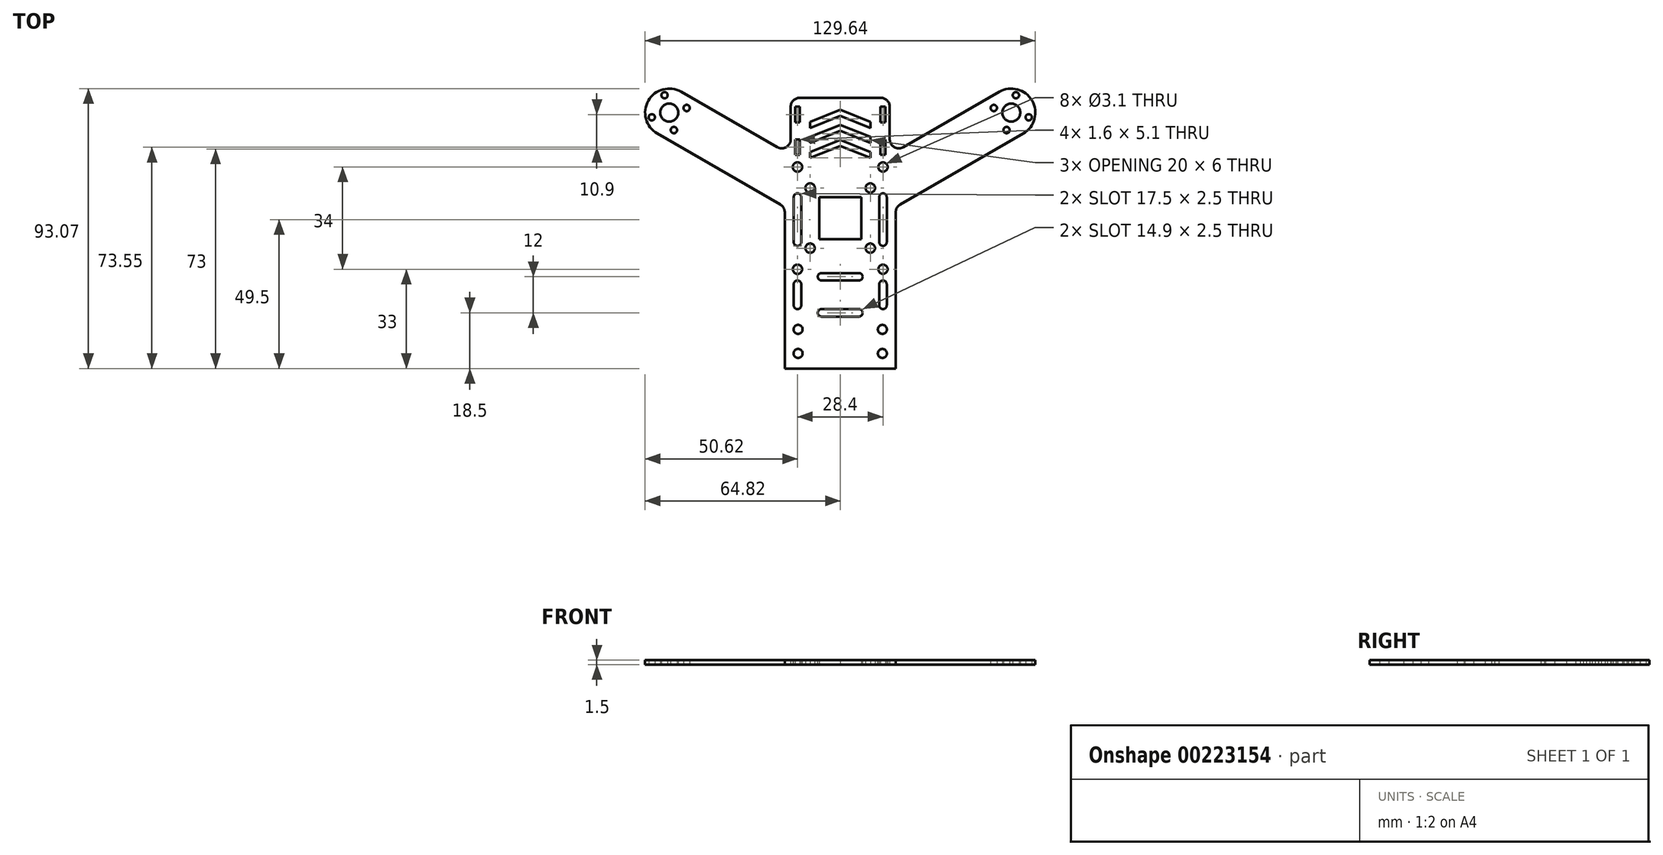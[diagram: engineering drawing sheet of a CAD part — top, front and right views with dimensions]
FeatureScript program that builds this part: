
annotation { "Feature Type Name" : "Feature", "Feature Type Description" : "" }
export const myFeature = defineFeature(function(context is Context, id is Id, definition is map)
    precondition{}
    {
        {
            var Q0;
            Q0=qCreatedBy(makeId("Top.planeOp"),FACE);
            var sketch = newSketch(context, id + "F0", { "sketchPlane" : qUnion([Q0])});
            skLineSegment(sketch, "E0.bottom", {"start": v(16.45, -32) * mm, "end": v(-16.45, -32) * mm});
            skLineSegment(sketch, "E0.top", {"start": v(16.45, 32) * mm, "end": v(-16.45, 32) * mm});
            skLineSegment(sketch, "E0.left", {"start": v(16.45, -32) * mm, "end": v(16.45, 32) * mm});
            skLineSegment(sketch, "E0.right", {"start": v(-16.45, -32) * mm, "end": v(-16.45, 32) * mm});
            skPoint(sketch, "E0.middle", {"position": v(0, 0) * mm});
            skLineSegment(sketch, "E1.bottom", {"start": v(-15, 29) * mm, "end": v(-13.4, 29) * mm});
            skLineSegment(sketch, "E1.top", {"start": v(-15, 23.9) * mm, "end": v(-13.4, 23.9) * mm});
            skLineSegment(sketch, "E1.left", {"start": v(-15, 29) * mm, "end": v(-15, 23.9) * mm});
            skLineSegment(sketch, "E1.right", {"start": v(-13.4, 29) * mm, "end": v(-13.4, 23.9) * mm});
            skLineSegment(sketch, "E2.bottom", {"start": v(15, 29) * mm, "end": v(13.4, 29) * mm});
            skLineSegment(sketch, "E2.top", {"start": v(15, 23.9) * mm, "end": v(13.4, 23.9) * mm});
            skLineSegment(sketch, "E2.left", {"start": v(15, 29) * mm, "end": v(15, 23.9) * mm});
            skLineSegment(sketch, "E2.right", {"start": v(13.4, 29) * mm, "end": v(13.4, 23.9) * mm});
            skLineSegment(sketch, "E3.bottom", {"start": v(-15, 18.1) * mm, "end": v(-13.4, 18.1) * mm});
            skLineSegment(sketch, "E3.top", {"start": v(-15, 13) * mm, "end": v(-13.4, 13) * mm});
            skLineSegment(sketch, "E3.left", {"start": v(-15, 18.1) * mm, "end": v(-15, 13) * mm});
            skLineSegment(sketch, "E3.right", {"start": v(-13.4, 18.1) * mm, "end": v(-13.4, 13) * mm});
            skLineSegment(sketch, "E4.bottom", {"start": v(13.4, 18.1) * mm, "end": v(15, 18.1) * mm});
            skLineSegment(sketch, "E4.top", {"start": v(13.4, 13) * mm, "end": v(15, 13) * mm});
            skLineSegment(sketch, "E4.left", {"start": v(13.4, 18.1) * mm, "end": v(13.4, 13) * mm});
            skLineSegment(sketch, "E4.right", {"start": v(15, 18.1) * mm, "end": v(15, 13) * mm});
            skCircle(sketch, "E5", {"center": v(-10, 2) * mm, "radius": 1.55 * mm});
            skCircle(sketch, "E6", {"center": v(10, 2) * mm, "radius": 1.55 * mm});
            skCircle(sketch, "E7", {"center": v(10, -18) * mm, "radius": 1.55 * mm});
            skCircle(sketch, "E8", {"center": v(-10, -18) * mm, "radius": 1.55 * mm});
            skLineSegment(sketch, "E9", {"start": v(0, 28) * mm, "end": v(-10, 24) * mm});
            skLineSegment(sketch, "E10", {"start": v(-10, 24) * mm, "end": v(-10, 22) * mm});
            skLineSegment(sketch, "E11", {"start": v(-10, 22) * mm, "end": v(0, 26) * mm});
            skLineSegment(sketch, "E12", {"start": v(0, 26) * mm, "end": v(10, 22) * mm});
            skLineSegment(sketch, "E13", {"start": v(10, 22) * mm, "end": v(10, 24) * mm});
            skLineSegment(sketch, "E14", {"start": v(10, 24) * mm, "end": v(0, 28) * mm});
            skLineSegment(sketch, "E15", {"start": v(0, 23) * mm, "end": v(-10, 19) * mm});
            skLineSegment(sketch, "E16", {"start": v(-10, 19) * mm, "end": v(-10, 17) * mm});
            skLineSegment(sketch, "E17", {"start": v(-10, 17) * mm, "end": v(0, 21) * mm});
            skLineSegment(sketch, "E18", {"start": v(0, 21) * mm, "end": v(10, 17) * mm});
            skLineSegment(sketch, "E19", {"start": v(10, 17) * mm, "end": v(10, 19) * mm});
            skLineSegment(sketch, "E20", {"start": v(10, 19) * mm, "end": v(0, 23) * mm});
            skLineSegment(sketch, "E21", {"start": v(0, 18) * mm, "end": v(-10, 14) * mm});
            skLineSegment(sketch, "E22", {"start": v(-10, 14) * mm, "end": v(-10, 12) * mm});
            skLineSegment(sketch, "E23", {"start": v(-10, 12) * mm, "end": v(0, 16) * mm});
            skLineSegment(sketch, "E24", {"start": v(0, 16) * mm, "end": v(10, 12) * mm});
            skLineSegment(sketch, "E25", {"start": v(10, 12) * mm, "end": v(10, 14) * mm});
            skLineSegment(sketch, "E26", {"start": v(10, 14) * mm, "end": v(0, 18) * mm});
            skCircle(sketch, "E27", {"center": v(14.2, 9) * mm, "radius": 1.55 * mm});
            skPoint(sketch, "E27.centerSnap0", {"position": v(14.2, 13) * mm});
            skCircle(sketch, "E28", {"center": v(-14.2, 9) * mm, "radius": 1.55 * mm});
            skPoint(sketch, "E28.centerSnap0", {"position": v(-14.2, 13) * mm});
            skCircle(sketch, "E29", {"center": v(-56.82, 27.07) * mm, "radius": 38.5 * mm, "construction": true});
            skCircle(sketch, "E30", {"center": v(56.82, 27.07) * mm, "radius": 38.5 * mm, "construction": true});
            skLineSegment(sketch, "E31", {"start": v(-52.82, 34) * mm, "end": v(-16.45, 13) * mm});
            skLineSegment(sketch, "E32", {"start": v(-52.82, 34) * mm, "end": v(-56.82, 27.07) * mm, "construction": true});
            skLineSegment(sketch, "E33", {"start": v(16.45, 13) * mm, "end": v(52.82, 34) * mm});
            skPoint(sketch, "E33.startSnap0", {"position": v(-10, 13) * mm});
            skLineSegment(sketch, "E34", {"start": v(52.82, 34) * mm, "end": v(56.82, 27.07) * mm, "construction": true});
            skArc(sketch, "E35", {"start": v(-52.82, 34) * mm, "mid": v(-63.75, 31.07) * mm, "end": v(-60.82, 20.14) * mm});
            skArc(sketch, "E36", {"start": v(52.82, 34) * mm, "mid": v(63.75, 31.07) * mm, "end": v(60.82, 20.14) * mm});
            skLineSegment(sketch, "E37", {"start": v(-56.82, 27.07) * mm, "end": v(-60.82, 20.14) * mm, "construction": true});
            skLineSegment(sketch, "E38", {"start": v(-60.82, 20.14) * mm, "end": v(-16.45, -5.48) * mm});
            skLineSegment(sketch, "E39", {"start": v(60.82, 20.14) * mm, "end": v(16.45, -5.48) * mm});
            skCircle(sketch, "E40", {"center": v(-56.82, 27.07) * mm, "radius": 3 * mm});
            skCircle(sketch, "E41", {"center": v(56.82, 27.07) * mm, "radius": 3 * mm});
            skCircle(sketch, "E42", {"center": v(56.82, 27.07) * mm, "radius": 6 * mm, "construction": true});
            skCircle(sketch, "E43", {"center": v(-56.82, 27.07) * mm, "radius": 6 * mm, "construction": true});
            skLineSegment(sketch, "E44", {"start": v(-59.65, 37.63) * mm, "end": v(-53.6, 15.03) * mm, "construction": true});
            skLineSegment(sketch, "E45", {"start": v(-69.83, 23.59) * mm, "end": v(-44.54, 30.36) * mm, "construction": true});
            skCircle(sketch, "E46", {"center": v(-58.38, 32.87) * mm, "radius": 1.05 * mm});
            skCircle(sketch, "E47", {"center": v(-51.03, 28.62) * mm, "radius": 1.05 * mm});
            skCircle(sketch, "E48", {"center": v(-62.62, 25.52) * mm, "radius": 1.05 * mm});
            skCircle(sketch, "E49", {"center": v(-55.27, 21.28) * mm, "radius": 1.05 * mm});
            skLineSegment(sketch, "E50", {"start": v(42.78, 30.83) * mm, "end": v(71.93, 23.02) * mm, "construction": true});
            skLineSegment(sketch, "E51", {"start": v(59.98, 38.85) * mm, "end": v(52.62, 11.38) * mm, "construction": true});
            skCircle(sketch, "E52", {"center": v(58.38, 32.87) * mm, "radius": 1.05 * mm});
            skCircle(sketch, "E53", {"center": v(62.62, 25.52) * mm, "radius": 1.05 * mm});
            skCircle(sketch, "E54", {"center": v(55.27, 21.28) * mm, "radius": 1.05 * mm});
            skCircle(sketch, "E55", {"center": v(51.03, 28.62) * mm, "radius": 1.05 * mm});
            skCircle(sketch, "E56", {"center": v(14.2, -25) * mm, "radius": 1.55 * mm});
            skCircle(sketch, "E57", {"center": v(-14.2, -25) * mm, "radius": 1.55 * mm});
            skLineSegment(sketch, "E58", {"start": v(16.45, -32) * mm, "end": v(16.45, -5.48) * mm});
            skLineSegment(sketch, "E59", {"start": v(18.45, -4.32) * mm, "end": v(18.45, -32) * mm});
            skLineSegment(sketch, "E60", {"start": v(18.45, -32) * mm, "end": v(16.45, -32) * mm});
            skLineSegment(sketch, "E61", {"start": v(-16.45, -32) * mm, "end": v(-16.45, -5.48) * mm});
            skLineSegment(sketch, "E62", {"start": v(-18.45, -4.32) * mm, "end": v(-18.45, -32) * mm});
            skLineSegment(sketch, "E63", {"start": v(-18.45, -32) * mm, "end": v(-16.45, -32) * mm});
            skLineSegment(sketch, "E64.bottom", {"start": v(-7, -1) * mm, "end": v(7, -1) * mm});
            skLineSegment(sketch, "E64.top", {"start": v(-7, -15) * mm, "end": v(7, -15) * mm});
            skLineSegment(sketch, "E64.left", {"start": v(-7, -1) * mm, "end": v(-7, -15) * mm});
            skLineSegment(sketch, "E64.right", {"start": v(7, -1) * mm, "end": v(7, -15) * mm});
            skLineSegment(sketch, "E65.bottom", {"start": v(-18.45, -32) * mm, "end": v(18.45, -32) * mm});
            skLineSegment(sketch, "E65.top", {"start": v(-18.45, -58) * mm, "end": v(18.45, -58) * mm});
            skLineSegment(sketch, "E65.left", {"start": v(-18.45, -32) * mm, "end": v(-18.45, -58) * mm});
            skLineSegment(sketch, "E65.right", {"start": v(18.45, -32) * mm, "end": v(18.45, -58) * mm});
            skSolve(sketch);
        }
        {
            var Q0;
            Q0 = qSketchRegion(id + "F0", true);
            extrude(context, id + "F1", {"entities" : qUnion([Q0]), "depth" : 1.5 * mm});
        }
        {
            var Q0;
            Q0=makeQuery(id+"F1.opExtrude","SWEPT_EDGE",EDGE,{"disambiguationData":[OSD([sQuery(id+"F0.wireOp",EDGE,"E0.right"),sQuery(id+"F0.wireOp",EDGE,"E31")])]});
            var Q1;
            Q1=makeQuery(id+"F1.opExtrude","SWEPT_EDGE",EDGE,{"disambiguationData":[OSD([sQuery(id+"F0.wireOp",EDGE,"E0.left"),sQuery(id+"F0.wireOp",EDGE,"E33")])]});
            var Q2;
            Q2=makeQuery(id+"F1.opExtrude","SWEPT_EDGE",EDGE,{"disambiguationData":[OSD([sQuery(id+"F0.wireOp",EDGE,"E0.left"),sQuery(id+"F0.wireOp",EDGE,"E39")])]});
            var Q3;
            Q3=makeQuery(id+"F1.opExtrude","SWEPT_EDGE",EDGE,{"disambiguationData":[OSD([sQuery(id+"F0.wireOp",EDGE,"E0.right"),sQuery(id+"F0.wireOp",EDGE,"E38")])]});
            fillet(context, id + "F2", {"entities" : qUnion([Q0, Q1, Q2, Q3]), "radius" : 3 * mm, "tangentPropagation" : true, "allowEdgeOverflow" : false});
        }
        {
            var Q0;
            Q0=makeQuery(id+"F1.opExtrude","CAP_FACE",FACE,{"disambiguationData":[OSD([sQuery(id+"F0.wireOp",EDGE,"E0.bottom"),sQuery(id+"F0.wireOp",EDGE,"E0.top"),sQuery(id+"F0.wireOp",EDGE,"E0.left"),sQuery(id+"F0.wireOp",EDGE,"E0.right"),sQuery(id+"F0.wireOp",EDGE,"E1.bottom"),sQuery(id+"F0.wireOp",EDGE,"E1.top"),sQuery(id+"F0.wireOp",EDGE,"E1.left"),sQuery(id+"F0.wireOp",EDGE,"E1.right"),sQuery(id+"F0.wireOp",EDGE,"E2.bottom"),sQuery(id+"F0.wireOp",EDGE,"E2.top"),sQuery(id+"F0.wireOp",EDGE,"E2.left"),sQuery(id+"F0.wireOp",EDGE,"E2.right"),sQuery(id+"F0.wireOp",EDGE,"E3.bottom"),sQuery(id+"F0.wireOp",EDGE,"E3.top"),sQuery(id+"F0.wireOp",EDGE,"E3.left"),sQuery(id+"F0.wireOp",EDGE,"E3.right"),sQuery(id+"F0.wireOp",EDGE,"E4.bottom"),sQuery(id+"F0.wireOp",EDGE,"E4.top"),sQuery(id+"F0.wireOp",EDGE,"E4.left"),sQuery(id+"F0.wireOp",EDGE,"E4.right"),sQuery(id+"F0.wireOp",EDGE,"E5"),sQuery(id+"F0.wireOp",EDGE,"E6"),sQuery(id+"F0.wireOp",EDGE,"E7"),sQuery(id+"F0.wireOp",EDGE,"E8"),sQuery(id+"F0.wireOp",EDGE,"E9"),sQuery(id+"F0.wireOp",EDGE,"E10"),sQuery(id+"F0.wireOp",EDGE,"E11"),sQuery(id+"F0.wireOp",EDGE,"E12"),sQuery(id+"F0.wireOp",EDGE,"E13"),sQuery(id+"F0.wireOp",EDGE,"E14"),sQuery(id+"F0.wireOp",EDGE,"E15"),sQuery(id+"F0.wireOp",EDGE,"E16"),sQuery(id+"F0.wireOp",EDGE,"E17"),sQuery(id+"F0.wireOp",EDGE,"E18"),sQuery(id+"F0.wireOp",EDGE,"E19"),sQuery(id+"F0.wireOp",EDGE,"E20"),sQuery(id+"F0.wireOp",EDGE,"E21"),sQuery(id+"F0.wireOp",EDGE,"E22"),sQuery(id+"F0.wireOp",EDGE,"E23"),sQuery(id+"F0.wireOp",EDGE,"E24"),sQuery(id+"F0.wireOp",EDGE,"E25"),sQuery(id+"F0.wireOp",EDGE,"E26"),sQuery(id+"F0.wireOp",EDGE,"E27"),sQuery(id+"F0.wireOp",EDGE,"E28"),sQuery(id+"F0.wireOp",EDGE,"E31"),sQuery(id+"F0.wireOp",EDGE,"E33"),sQuery(id+"F0.wireOp",EDGE,"E35"),sQuery(id+"F0.wireOp",EDGE,"E36"),sQuery(id+"F0.wireOp",EDGE,"E38"),sQuery(id+"F0.wireOp",EDGE,"E39"),sQuery(id+"F0.wireOp",EDGE,"E40"),sQuery(id+"F0.wireOp",EDGE,"E41"),sQuery(id+"F0.wireOp",EDGE,"E46"),sQuery(id+"F0.wireOp",EDGE,"E47"),sQuery(id+"F0.wireOp",EDGE,"E48"),sQuery(id+"F0.wireOp",EDGE,"E49"),sQuery(id+"F0.wireOp",EDGE,"E52"),sQuery(id+"F0.wireOp",EDGE,"E53"),sQuery(id+"F0.wireOp",EDGE,"E54"),sQuery(id+"F0.wireOp",EDGE,"E55"),sQuery(id+"F0.wireOp",EDGE,"E56"),sQuery(id+"F0.wireOp",EDGE,"E57"),sQuery(id+"F0.wireOp",EDGE,"E59"),sQuery(id+"F0.wireOp",EDGE,"E60"),sQuery(id+"F0.wireOp",EDGE,"E62"),sQuery(id+"F0.wireOp",EDGE,"E63")])],"isStart":false});
            var sketch = newSketch(context, id + "F3", { "sketchPlane" : qUnion([Q0])});
            skLineSegment(sketch, "E66", {"start": v(-14.2, -25) * mm, "end": v(14.2, -25) * mm, "construction": true});
            skLineSegment(sketch, "E67", {"start": v(-14.2, -1) * mm, "end": v(-14.2, -16) * mm});
            skLineSegment(sketch, "E68", {"start": v(14.2, -1) * mm, "end": v(14.2, -16) * mm});
            skArc(sketch, "E69.0.startCap", {"start": v(-15.45, -1) * mm, "mid": v(-14.2, 0.25) * mm, "end": v(-12.95, -1) * mm});
            skArc(sketch, "E69.0.endCap", {"start": v(-12.95, -16) * mm, "mid": v(-14.2, -17.25) * mm, "end": v(-15.45, -16) * mm});
            skLineSegment(sketch, "E69.0.left", {"start": v(-12.95, -1) * mm, "end": v(-12.95, -16) * mm});
            skLineSegment(sketch, "E69.0.right", {"start": v(-15.45, -1) * mm, "end": v(-15.45, -16) * mm});
            skArc(sketch, "E70.0.startCap", {"start": v(12.95, -1) * mm, "mid": v(14.2, 0.25) * mm, "end": v(15.45, -1) * mm});
            skArc(sketch, "E70.0.endCap", {"start": v(15.45, -16) * mm, "mid": v(14.2, -17.25) * mm, "end": v(12.95, -16) * mm});
            skLineSegment(sketch, "E70.0.left", {"start": v(15.45, -1) * mm, "end": v(15.45, -16) * mm});
            skLineSegment(sketch, "E70.0.right", {"start": v(12.95, -1) * mm, "end": v(12.95, -16) * mm});
            skLineSegment(sketch, "E71", {"start": v(-14.2, -30) * mm, "end": v(-14.2, -37) * mm});
            skLineSegment(sketch, "E72", {"start": v(14.2, -30) * mm, "end": v(14.2, -37) * mm});
            skArc(sketch, "E73.0.startCap", {"start": v(-15.45, -30) * mm, "mid": v(-14.2, -28.75) * mm, "end": v(-12.95, -30) * mm});
            skArc(sketch, "E73.0.endCap", {"start": v(-12.95, -37) * mm, "mid": v(-14.2, -38.25) * mm, "end": v(-15.45, -37) * mm});
            skLineSegment(sketch, "E73.0.left", {"start": v(-12.95, -30) * mm, "end": v(-12.95, -37) * mm});
            skLineSegment(sketch, "E73.0.right", {"start": v(-15.45, -30) * mm, "end": v(-15.45, -37) * mm});
            skArc(sketch, "E74.0.startCap", {"start": v(12.95, -30) * mm, "mid": v(14.2, -28.75) * mm, "end": v(15.45, -30) * mm});
            skArc(sketch, "E74.0.endCap", {"start": v(15.45, -37) * mm, "mid": v(14.2, -38.25) * mm, "end": v(12.95, -37) * mm});
            skLineSegment(sketch, "E74.0.left", {"start": v(15.45, -30) * mm, "end": v(15.45, -37) * mm});
            skLineSegment(sketch, "E74.0.right", {"start": v(12.95, -30) * mm, "end": v(12.95, -37) * mm});
            skCircle(sketch, "E75", {"center": v(-14, -45) * mm, "radius": 1.5 * mm});
            skPoint(sketch, "E75.centerSnap0", {"position": v(-14.2, -38.25) * mm});
            skCircle(sketch, "E76", {"center": v(-14, -53) * mm, "radius": 1.5 * mm});
            skCircle(sketch, "E77", {"center": v(14, -45) * mm, "radius": 1.5 * mm});
            skPoint(sketch, "E77.centerSnap0", {"position": v(14.2, -38.25) * mm});
            skCircle(sketch, "E78", {"center": v(14, -53) * mm, "radius": 1.5 * mm});
            skLineSegment(sketch, "E79", {"start": v(-6.2, -27.5) * mm, "end": v(6.2, -27.5) * mm});
            skLineSegment(sketch, "E80", {"start": v(-6.2, -39.5) * mm, "end": v(6.2, -39.5) * mm});
            skArc(sketch, "E81.0.startCap", {"start": v(-6.2, -28.75) * mm, "mid": v(-7.45, -27.5) * mm, "end": v(-6.2, -26.25) * mm});
            skArc(sketch, "E81.0.endCap", {"start": v(6.2, -26.25) * mm, "mid": v(7.45, -27.5) * mm, "end": v(6.2, -28.75) * mm});
            skLineSegment(sketch, "E81.0.left", {"start": v(-6.2, -26.25) * mm, "end": v(6.2, -26.25) * mm});
            skLineSegment(sketch, "E81.0.right", {"start": v(-6.2, -28.75) * mm, "end": v(6.2, -28.75) * mm});
            skArc(sketch, "E82.0.startCap", {"start": v(-6.2, -40.75) * mm, "mid": v(-7.45, -39.5) * mm, "end": v(-6.2, -38.25) * mm});
            skArc(sketch, "E82.0.endCap", {"start": v(6.2, -38.25) * mm, "mid": v(7.45, -39.5) * mm, "end": v(6.2, -40.75) * mm});
            skLineSegment(sketch, "E82.0.left", {"start": v(-6.2, -38.25) * mm, "end": v(6.2, -38.25) * mm});
            skLineSegment(sketch, "E82.0.right", {"start": v(-6.2, -40.75) * mm, "end": v(6.2, -40.75) * mm});
            skSolve(sketch);
        }
        {
            var Q0;
            Q0 = qSketchRegion(id + "F3", true);
            extrude(context, id + "F4", {"entities" : qUnion([Q0]), "operationType" : NewBodyOperationType.REMOVE, "endBound" : BoundingType.THROUGH_ALL, "oppositeDirection" : true, "depth" : 25 * mm});
        }
    });
